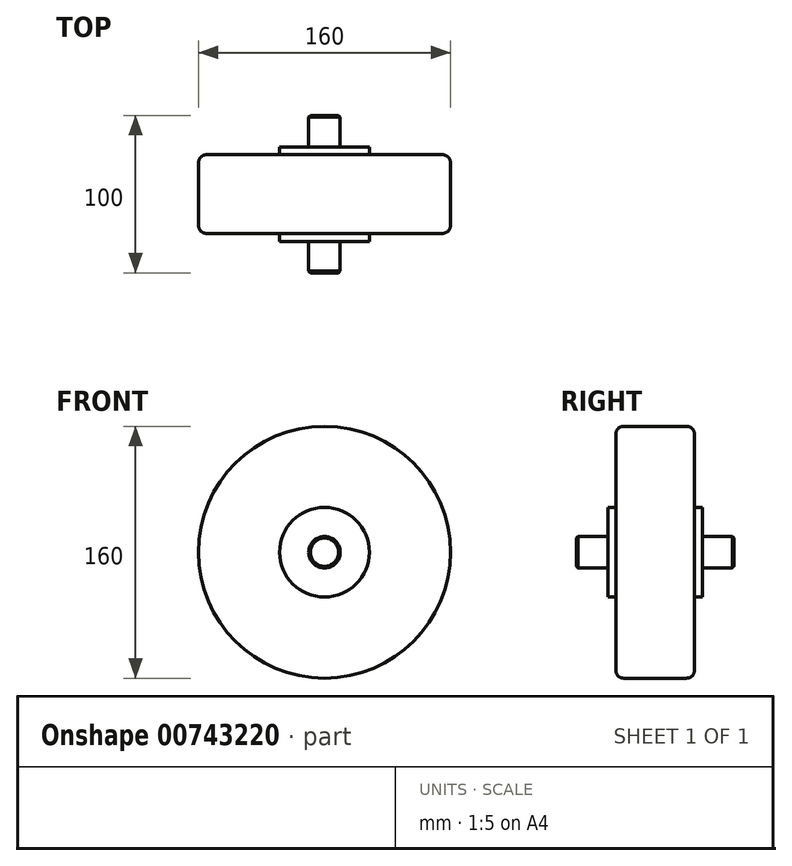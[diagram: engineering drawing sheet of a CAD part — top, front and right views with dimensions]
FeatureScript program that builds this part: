
annotation { "Feature Type Name" : "Feature", "Feature Type Description" : "" }
export const myFeature = defineFeature(function(context is Context, id is Id, definition is map)
    precondition{}
    {
        {
            var Q0;
            Q0=qCreatedBy(makeId("Front.planeOp"),FACE);
            var sketch = newSketch(context, id + "F0", { "sketchPlane" : qUnion([Q0])});
            skCircle(sketch, "E0", {"center": v(0, 0) * mm, "radius": 80 * mm});
            skCircle(sketch, "E1", {"center": v(0, 0) * mm, "radius": 75 * mm});
            skCircle(sketch, "E2", {"center": v(0, 0) * mm, "radius": 10 * mm});
            skCircle(sketch, "E3", {"center": v(0, 0) * mm, "radius": 28.5 * mm});
            skSolve(sketch);
        }
        {
            var Q0;
            Q0=makeQuery(id+"F0.imprint","IMPRINT",FACE,{"disambiguationData":[TD([[makeQuery(id+"F0.imprint","IMPRINT",EDGE,{"derivedFrom":sQuery(id+"F0.wireOp",EDGE,"E0")}),1.0]])]});
            var Q1;
            Q1=makeQuery(id+"F0.imprint","IMPRINT",FACE,{"disambiguationData":[TD([[makeQuery(id+"F0.imprint","IMPRINT",EDGE,{"derivedFrom":sQuery(id+"F0.wireOp",EDGE,"E1")}),1.0]])]});
            extrude(context, id + "F1", {"entities" : qUnion([Q0, Q1]), "depth" : 50 * mm, "offsetDistance" : 25 * mm, "symmetric" : true});
        }
        {
            var Q0;
            Q0=makeQuery(id+"F0.imprint","IMPRINT",FACE,{"disambiguationData":[TD([[makeQuery(id+"F0.imprint","IMPRINT",EDGE,{"derivedFrom":sQuery(id+"F0.wireOp",EDGE,"E2")}),-1.0]])]});
            extrude(context, id + "F2", {"entities" : qUnion([Q0]), "operationType" : NewBodyOperationType.ADD, "depth" : 60 * mm, "offsetDistance" : 25 * mm, "symmetric" : true});
        }
        {
            var Q0;
            Q0=makeQuery(id+"F0.imprint","IMPRINT",FACE,{"disambiguationData":[TD([[makeQuery(id+"F0.imprint","IMPRINT",EDGE,{"derivedFrom":sQuery(id+"F0.wireOp",EDGE,"E2")}),1.0]])]});
            extrude(context, id + "F3", {"entities" : qUnion([Q0]), "operationType" : NewBodyOperationType.ADD, "depth" : 100 * mm, "offsetDistance" : 25 * mm, "symmetric" : true});
        }
        {
            var Q0;
            Q0=makeQuery(id+"F1.opExtrude","CAP_EDGE",EDGE,{"disambiguationData":[OSD([sQuery(id+"F0.wireOp",EDGE,"E0")])],"isStart":false});
            var Q1;
            Q1=makeQuery(id+"F1.opExtrude","CAP_EDGE",EDGE,{"disambiguationData":[OSD([sQuery(id+"F0.wireOp",EDGE,"E0")])],"isStart":true});
            fillet(context, id + "F4", {"entities" : qUnion([Q0, Q1]), "tangentPropagation" : true, "radius" : 5 * mm, "defaultsChanged" : false, "vertexSettings" : [], "allowEdgeOverflow" : false});
        }
        {
            var Q0;
            Q0=makeQuery(id+"F3.opExtrude","CAP_EDGE",EDGE,{"disambiguationData":[OSD([sQuery(id+"F0.wireOp",EDGE,"E2")])],"isStart":false});
            var Q1;
            Q1=makeQuery(id+"F3.opExtrude","CAP_EDGE",EDGE,{"disambiguationData":[OSD([sQuery(id+"F0.wireOp",EDGE,"E2")])],"isStart":true});
            chamfer(context, id + "F5", {"entities" : qUnion([Q0, Q1]), "width" : 1 * mm, "tangentPropagation" : true});
        }
    });
